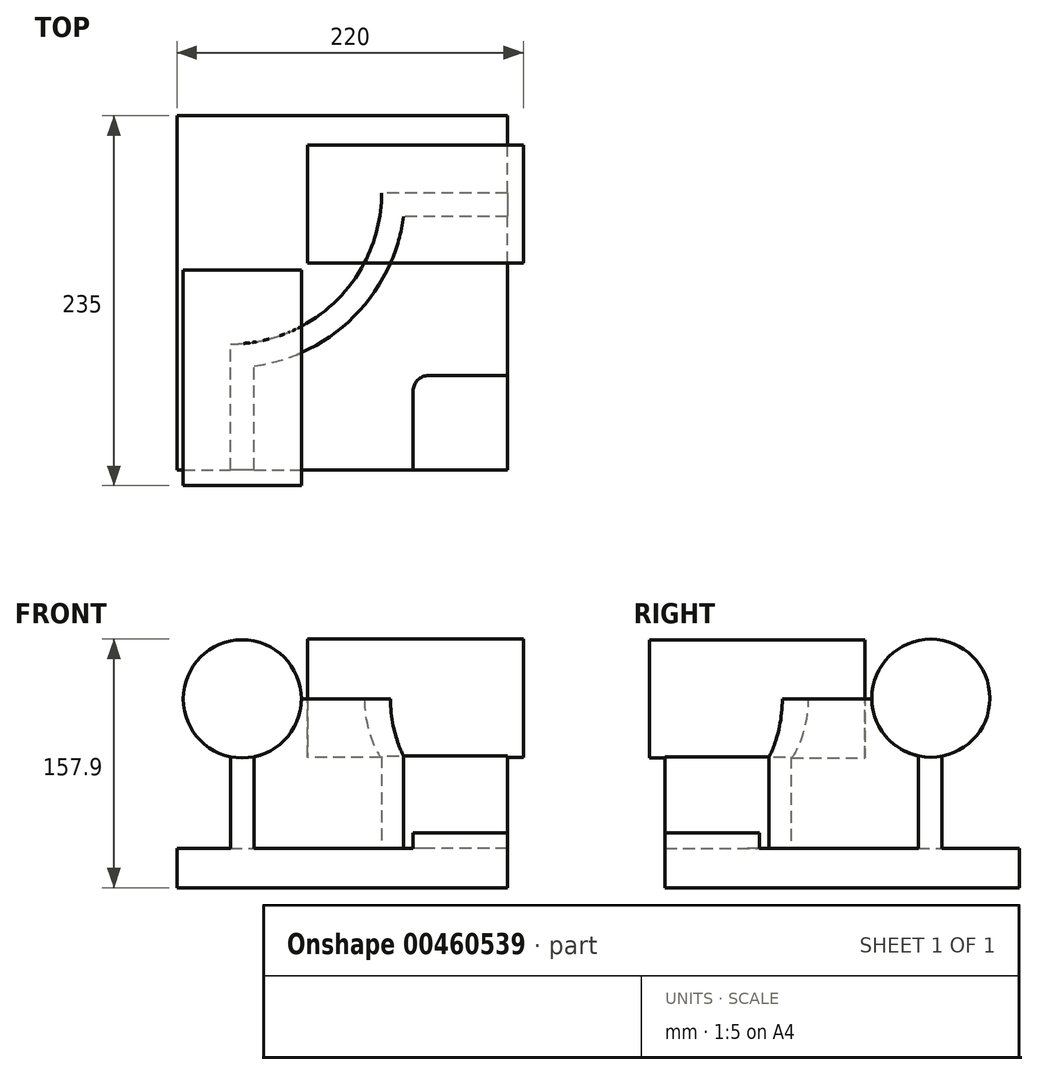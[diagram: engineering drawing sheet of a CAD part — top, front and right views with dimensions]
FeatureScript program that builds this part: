
annotation { "Feature Type Name" : "Feature", "Feature Type Description" : "" }
export const myFeature = defineFeature(function(context is Context, id is Id, definition is map)
    precondition{}
    {
        {
            var Q0;
            Q0=qCreatedBy(makeId("Top.planeOp"),FACE);
            var sketch = newSketch(context, id + "F0", { "sketchPlane" : qUnion([Q0])});
            skLineSegment(sketch, "E0.bottom", {"start": v(-105, -112.5) * mm, "end": v(105, -112.5) * mm});
            skLineSegment(sketch, "E0.top", {"start": v(-105, 112.5) * mm, "end": v(105, 112.5) * mm});
            skLineSegment(sketch, "E0.left", {"start": v(-105, -112.5) * mm, "end": v(-105, 112.5) * mm});
            skLineSegment(sketch, "E0.right", {"start": v(105, -112.5) * mm, "end": v(105, 112.5) * mm});
            skPoint(sketch, "E0.middle", {"position": v(0, 0) * mm});
            skSolve(sketch);
        }
        {
            var Q0;
            Q0 = qSketchRegion(id + "F0", true);
            extrude(context, id + "F1", {"entities" : qUnion([Q0]), "depth" : 25 * mm});
        }
        {
            var Q0;
            Q0=makeQuery(id+"F1.opExtrude","CAP_FACE",FACE,{"disambiguationData":[OSD([sQuery(id+"F0.wireOp",EDGE,"E0.bottom"),sQuery(id+"F0.wireOp",EDGE,"E0.top"),sQuery(id+"F0.wireOp",EDGE,"E0.left"),sQuery(id+"F0.wireOp",EDGE,"E0.right")])],"isStart":false});
            var sketch = newSketch(context, id + "F2", { "sketchPlane" : qUnion([Q0])});
            skLineSegment(sketch, "E1", {"start": v(-71, -112.5) * mm, "end": v(-71, -32.5) * mm});
            skLineSegment(sketch, "E2", {"start": v(105, 63.5) * mm, "end": v(25, 63.5) * mm});
            skArc(sketch, "E3", {"start": v(-71, -32.5) * mm, "mid": v(-3.12, -4.38) * mm, "end": v(25, 63.5) * mm});
            skLineSegment(sketch, "E4", {"start": v(-71, 63.5) * mm, "end": v(25, 63.5) * mm, "construction": true});
            skLineSegment(sketch, "E5", {"start": v(-71, 63.5) * mm, "end": v(-71, -32.5) * mm, "construction": true});
            skLineSegment(sketch, "E6.0", {"start": v(-56, -112.5) * mm, "end": v(-56, -46.48) * mm});
            skArc(sketch, "E6.1", {"start": v(-56, -46.48) * mm, "mid": v(7.49, -14.99) * mm, "end": v(38.98, 48.5) * mm});
            skLineSegment(sketch, "E6.2", {"start": v(105, 48.5) * mm, "end": v(38.98, 48.5) * mm});
            skLineSegment(sketch, "E7.0", {"start": v(105, -112.5) * mm, "end": v(105, 112.5) * mm});
            skLineSegment(sketch, "E8.0", {"start": v(-105, -112.5) * mm, "end": v(105, -112.5) * mm});
            skSolve(sketch);
        }
        {
            var Q0;
            {var subQ2=sQuery(id+"F2.wireOp",EDGE,"E1");Q0=makeQuery(id+"F2.imprint","IMPRINT",FACE,{"disambiguationData":[TD([[makeQuery(id+"F2.imprint","IMPRINT",EDGE,{"derivedFrom":subQ2}),-1.0]])]});}
            extrude(context, id + "F3", {"entities" : qUnion([Q0]), "operationType" : NewBodyOperationType.ADD, "depth" : 95 * mm});
        }
        {
            var Q0;
            Q0=makeQuery(id+"F3.boolean.opBoolean","MERGE",FACE,{"derivedFrom":[makeQuery(id+"F1.opExtrude","SWEPT_FACE",FACE,{"disambiguationData":[OSD([sQuery(id+"F0.wireOp",EDGE,"E0.bottom")])]}),makeQuery(id+"F3.opExtrude","SWEPT_FACE",FACE,{"disambiguationData":[OSD([sQuery(id+"F2.wireOp",EDGE,"E8.0")])]})]});
            var sketch = newSketch(context, id + "F4", { "sketchPlane" : qUnion([Q0])});
            skCircle(sketch, "E9", {"center": v(-63.5, 120) * mm, "radius": 37.5 * mm});
            skSolve(sketch);
        }
        {
            var Q0;
            Q0 = qSketchRegion(id + "F4", true);
            extrude(context, id + "F5", {"entities" : qUnion([Q0]), "operationType" : NewBodyOperationType.ADD, "depth" : 10 * mm, "hasSecondDirection" : true, "secondDirectionOppositeDirection" : true, "secondDirectionDepth" : 127 * mm});
        }
        {
            var Q0;
            Q0=makeQuery(id+"F3.boolean.opBoolean","MERGE",FACE,{"derivedFrom":[makeQuery(id+"F1.opExtrude","SWEPT_FACE",FACE,{"disambiguationData":[OSD([sQuery(id+"F0.wireOp",EDGE,"E0.right")])]}),makeQuery(id+"F3.opExtrude","SWEPT_FACE",FACE,{"disambiguationData":[OSD([sQuery(id+"F2.wireOp",EDGE,"E7.0")])]})]});
            var sketch = newSketch(context, id + "F6", { "sketchPlane" : qUnion([Q0])});
            skCircle(sketch, "E10", {"center": v(56.3, 120.4) * mm, "radius": 37.5 * mm});
            skSolve(sketch);
        }
        {
            var Q0;
            Q0 = qSketchRegion(id + "F6", true);
            extrude(context, id + "F7", {"entities" : qUnion([Q0]), "operationType" : NewBodyOperationType.ADD, "depth" : 10 * mm, "hasSecondDirection" : true, "secondDirectionOppositeDirection" : true, "secondDirectionDepth" : 127 * mm});
        }
        {
            var Q0;
            {var subQ0=sQuery(id+"F0.wireOp",EDGE,"E0.right");var subQ1=sQuery(id+"F0.wireOp",EDGE,"E0.bottom");Q0=makeQuery(id+"F3.boolean.opBoolean","SPLIT",FACE,{"disambiguationData":[TD([makeQuery(id+"F3.opExtrude","SWEPT_FACE",FACE,{"disambiguationData":[OSD([sQuery(id+"F2.wireOp",EDGE,"E6.0")])]})])],"derivedFrom":makeQuery(id+"F1.opExtrude","CAP_FACE",FACE,{"disambiguationData":[OSD([subQ1,sQuery(id+"F0.wireOp",EDGE,"E0.top"),sQuery(id+"F0.wireOp",EDGE,"E0.left"),subQ0])],"isStart":false})});}
            var sketch = newSketch(context, id + "F8", { "sketchPlane" : qUnion([Q0])});
            skLineSegment(sketch, "E11.bottom", {"start": v(105, -112.5) * mm, "end": v(45, -112.5) * mm});
            skLineSegment(sketch, "E11.top", {"start": v(105, -52.5) * mm, "end": v(45, -52.5) * mm});
            skLineSegment(sketch, "E11.left", {"start": v(105, -112.5) * mm, "end": v(105, -52.5) * mm});
            skLineSegment(sketch, "E11.right", {"start": v(45, -112.5) * mm, "end": v(45, -52.5) * mm});
            skSolve(sketch);
        }
        {
            var Q0;
            Q0 = qSketchRegion(id + "F8", true);
            extrude(context, id + "F9", {"entities" : qUnion([Q0]), "operationType" : NewBodyOperationType.ADD, "depth" : 10 * mm});
        }
        {
            var Q0;
            Q0=makeQuery(id+"F9.opExtrude","SWEPT_EDGE",EDGE,{"disambiguationData":[OSD([sQuery(id+"F8.wireOp",EDGE,"E11.top"),sQuery(id+"F8.wireOp",EDGE,"E11.right")])]});
            fillet(context, id + "F10", {"entities" : qUnion([Q0]), "radius" : 10 * mm, "tangentPropagation" : true, "allowEdgeOverflow" : false});
        }
    });
